# Revit family: 3031854 Lighting Fixture_Sylvania_Syl-Lighter II_Ceiling Recessed
name_source: partatom
category: Lighting Fixtures
revit_build: Autodesk Revit 2017 (Build: 20190507_1515(x64)
units: mm (PartAtom-declared; Revit-internal decimal feet)

## family parameters
Cut with Voids When Loaded = No
Host = Face
Light Source = Yes
OmniClass Number = 23.80.70.11.17
OmniClass Title = Specialized Lighting by Location or Use
Part Type = Normal
Room Calculation Point = No
Round Connector Dimension = Use Diameter
Shared = No

## types (1)
- Syl-Lighter LED II 220 RO 21W NW 1-10V
    Accessory Diameter = 220 mm  [stored 0.721785 ft]
    Accessory Material = Aluminum_Sylvania_Syl-Lighter LED II_White_RAL 9003
    Accessory Radius = 110 mm  [stored 0.360892 ft]
    Apparent Load = 21 VA
    Assembly Code = D5020200
    Beam Angle = 74.00°
    Body Material = Metal_Sylvania_Syl-Lighter LED II_Silver
    Catalog Number = 3031854 Syl-Lighter LED II 220 RO 21W NW 1-10V
    Color Filter = 16777215
    Cutout Diameter = 205 mm  [stored 0.672572 ft]
    Default Elevation = 0 mm  [stored 0 ft]
    Description = Ceiling recessed IP44 LED downlight, perfect where limited ceiling void is available with only 60mm product depth and 205mm cutout. Ideal replacement for 1x42W CFL downlights. The polycarbonate diffuser allows for a wider light distribution and increased spacings between luminiares. Loop in loop out connector allows for quick installation. Die-cast aluminium body, 2071LM, 21W, 99lm/W, 4000K, Driver Current: 600mA, CRI80, 74° beam angle, 1-10V dimmable LED driver, IP44, IK07, 50,000 hrs (L70), (HxW) 60x205mm, 5 step MacAdam ellipse, 0.60kg, RAL9003, Class 2, 220-240V, energy class: A++, A+, A
    Diameter = 205 mm  [stored 0.672572 ft]
    Diffuser Diameter = 185 mm  [stored 0.606955 ft]
    Diffuser Material = Polycarbonate_Sylvania_Syl-Lighter LED II_Opal
    Diffuser Radius = 92.5 mm  [stored 0.303478 ft]
    Dimmable = DALI
    Dimming Lamp Color Temperature Shift = <None>
    Drive Current = 600mA
    Electrical Protection = CLASS II
    Emit Shape Visible in Rendering = No
    Emit from Circle Diameter = 185 mm  [stored 0.606955 ft]
    Energy Class = A++, A+, A
    Glow Wire Test = 650 °C
    Height = 60 mm  [stored 0.19685 ft]
    IK Rating = IK07
    IP Rating = IP44
    Inner Diameter = 201 mm  [stored 0.659449 ft]
    Lamp = LED
    Lamp Comments = Integrated LED
    Life = 50 000h
    Manufacturer = Feilo Sylvania
    Model = Syl-Lighter LED II 220 RO 21W NW 1-10V
    Photometric Web File = 3031854.ies
    Product Family = SYL-LIGHTER LED II
    Product Page URL = http://www.sylvania-lighting.com
    Recessed Depth = 60 mm  [stored 0.19685 ft]
    Ta Rating = -10°C to +40°C
    Tilt Angle = -90.00°
    URL = http://www.sylvania-lighting.com
    Voltage = 240 V
    Voltage Comments = UNV (Universal Voltage; 220-240 Volt)
    Weight = 0.60 kg

note: [stored X ft] marks values corroborated as IEEE doubles in the binary element streams (Revit-internal decimal feet)

## geometry (parser evidence)
native form markers: Blend x4, Sweep x2
no freeform markers — native parametric forms only
